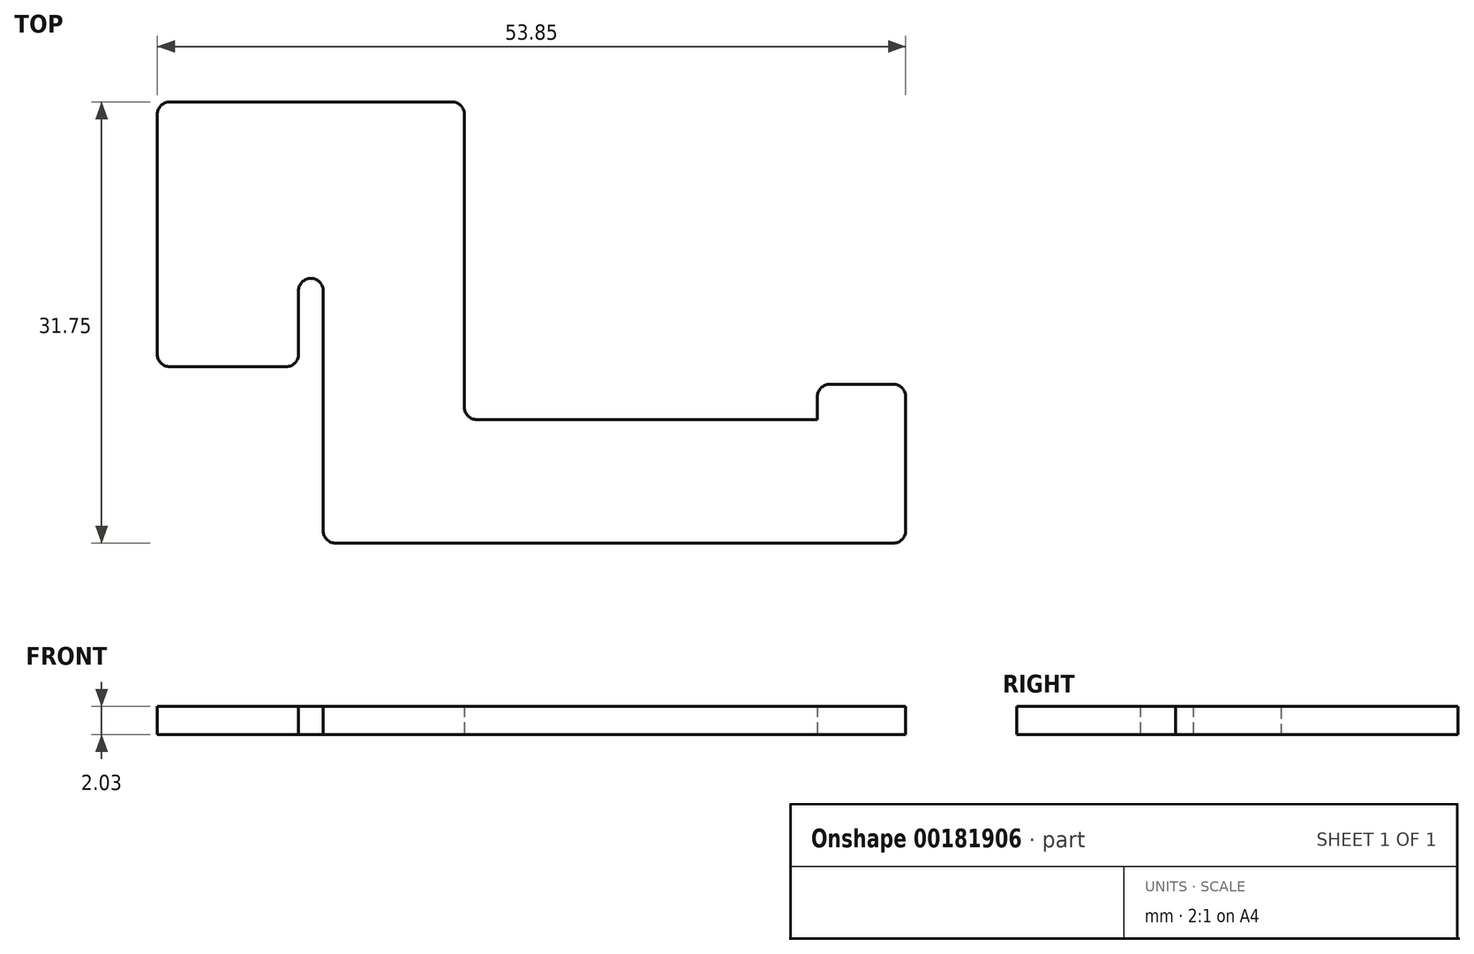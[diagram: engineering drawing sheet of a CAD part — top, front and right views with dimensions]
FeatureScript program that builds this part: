
annotation { "Feature Type Name" : "Feature", "Feature Type Description" : "" }
export const myFeature = defineFeature(function(context is Context, id is Id, definition is map)
    precondition{}
    {
        {
            var Q0;
            Q0=qCreatedBy(makeId("Top.planeOp"),FACE);
            var sketch = newSketch(context, id + "F0", { "sketchPlane" : qUnion([Q0])});
            skLineSegment(sketch, "E0", {"start": v(-10.16, 12.7) * mm, "end": v(-10.16, -6.35) * mm});
            skLineSegment(sketch, "E1", {"start": v(-10.16, -6.35) * mm, "end": v(0, -6.35) * mm});
            skLineSegment(sketch, "E2", {"start": v(0, -6.35) * mm, "end": v(0, 0) * mm});
            skLineSegment(sketch, "E3", {"start": v(0, 0) * mm, "end": v(1.78, 0) * mm});
            skLineSegment(sketch, "E4", {"start": v(1.78, 0) * mm, "end": v(1.78, -19.05) * mm});
            skLineSegment(sketch, "E5", {"start": v(1.78, -19.05) * mm, "end": v(43.69, -19.05) * mm});
            skLineSegment(sketch, "E6", {"start": v(43.69, -19.05) * mm, "end": v(43.69, -7.62) * mm});
            skLineSegment(sketch, "E7", {"start": v(43.69, -7.62) * mm, "end": v(37.34, -7.62) * mm});
            skLineSegment(sketch, "E8", {"start": v(37.34, -7.62) * mm, "end": v(37.34, -10.16) * mm});
            skLineSegment(sketch, "E9", {"start": v(37.34, -10.16) * mm, "end": v(11.94, -10.16) * mm});
            skLineSegment(sketch, "E10", {"start": v(11.94, -10.16) * mm, "end": v(11.94, 12.7) * mm});
            skLineSegment(sketch, "E11", {"start": v(11.94, 12.7) * mm, "end": v(-10.16, 12.7) * mm});
            skLineSegment(sketch, "E12", {"start": v(1.78, 0) * mm, "end": v(11.94, 0) * mm, "construction": true});
            skSolve(sketch);
        }
        {
            var Q0;
            Q0 = qSketchRegion(id + "F0", true);
            extrude(context, id + "F1", {"entities" : qUnion([Q0]), "depth" : 2.03 * mm});
        }
        {
            var Q0;
            Q0=makeQuery(id+"F1.opExtrude","SWEPT_EDGE",EDGE,{"disambiguationData":[OSD([sQuery(id+"F0.wireOp",EDGE,"E0"),sQuery(id+"F0.wireOp",EDGE,"E1")])]});
            var Q1;
            Q1=makeQuery(id+"F1.opExtrude","SWEPT_EDGE",EDGE,{"disambiguationData":[OSD([sQuery(id+"F0.wireOp",EDGE,"E1"),sQuery(id+"F0.wireOp",EDGE,"E2")])]});
            var Q2;
            Q2=makeQuery(id+"F1.opExtrude","SWEPT_EDGE",EDGE,{"disambiguationData":[OSD([sQuery(id+"F0.wireOp",EDGE,"E2"),sQuery(id+"F0.wireOp",EDGE,"E3")])]});
            var Q3;
            Q3=makeQuery(id+"F1.opExtrude","SWEPT_EDGE",EDGE,{"disambiguationData":[OSD([sQuery(id+"F0.wireOp",EDGE,"E3"),sQuery(id+"F0.wireOp",EDGE,"E4")])]});
            var Q4;
            Q4=makeQuery(id+"F1.opExtrude","SWEPT_EDGE",EDGE,{"disambiguationData":[OSD([sQuery(id+"F0.wireOp",EDGE,"E4"),sQuery(id+"F0.wireOp",EDGE,"E5")])]});
            var Q5;
            Q5=makeQuery(id+"F1.opExtrude","SWEPT_EDGE",EDGE,{"disambiguationData":[OSD([sQuery(id+"F0.wireOp",EDGE,"E0"),sQuery(id+"F0.wireOp",EDGE,"E11")])]});
            var Q6;
            Q6=makeQuery(id+"F1.opExtrude","SWEPT_EDGE",EDGE,{"disambiguationData":[OSD([sQuery(id+"F0.wireOp",EDGE,"E7"),sQuery(id+"F0.wireOp",EDGE,"E8")])]});
            var Q7;
            Q7=makeQuery(id+"F1.opExtrude","SWEPT_EDGE",EDGE,{"disambiguationData":[OSD([sQuery(id+"F0.wireOp",EDGE,"E5"),sQuery(id+"F0.wireOp",EDGE,"E6")])]});
            var Q8;
            Q8=makeQuery(id+"F1.opExtrude","SWEPT_EDGE",EDGE,{"disambiguationData":[OSD([sQuery(id+"F0.wireOp",EDGE,"E10"),sQuery(id+"F0.wireOp",EDGE,"E11")])]});
            var Q9;
            Q9=makeQuery(id+"F1.opExtrude","SWEPT_EDGE",EDGE,{"disambiguationData":[OSD([sQuery(id+"F0.wireOp",EDGE,"E9"),sQuery(id+"F0.wireOp",EDGE,"E10")])]});
            var Q10;
            Q10=makeQuery(id+"F1.opExtrude","SWEPT_EDGE",EDGE,{"disambiguationData":[OSD([sQuery(id+"F0.wireOp",EDGE,"E6"),sQuery(id+"F0.wireOp",EDGE,"E7")])]});
            fillet(context, id + "F2", {"entities" : qUnion([Q0, Q1, Q2, Q3, Q4, Q5, Q6, Q7, Q8, Q9, Q10]), "radius" : 0.89 * mm, "tangentPropagation" : true, "allowEdgeOverflow" : false});
        }
    });
